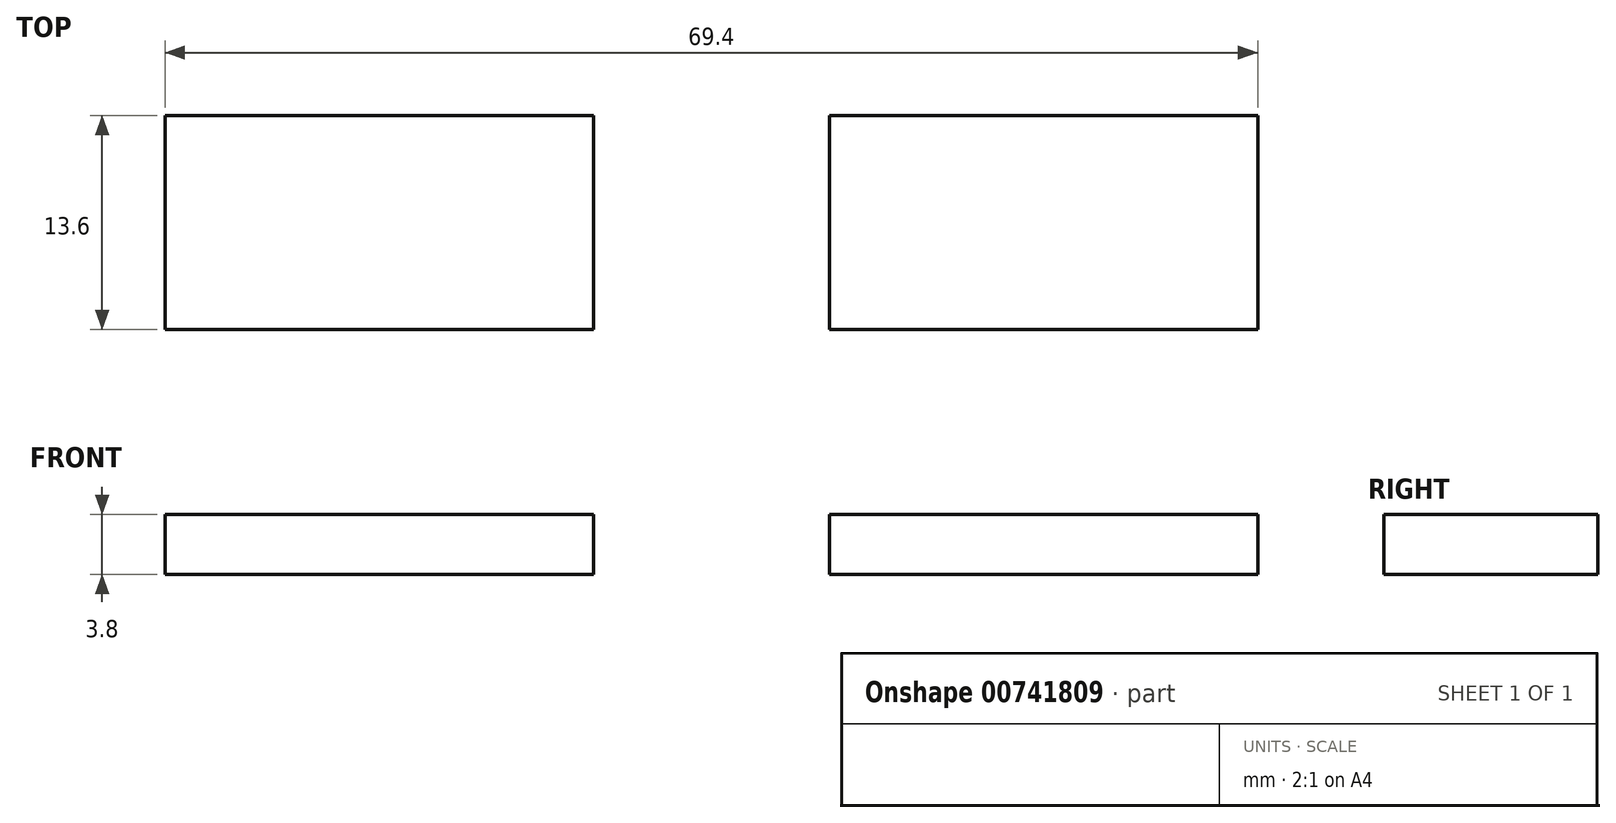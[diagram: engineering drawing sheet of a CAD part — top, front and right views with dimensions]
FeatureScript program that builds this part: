
annotation { "Feature Type Name" : "Feature", "Feature Type Description" : "" }
export const myFeature = defineFeature(function(context is Context, id is Id, definition is map)
    precondition{}
    {
        {
            var Q0;
            Q0=qCreatedBy(makeId("Top.planeOp"),FACE);
            var sketch = newSketch(context, id + "F0", { "sketchPlane" : qUnion([Q0])});
            skLineSegment(sketch, "E0.bottom", {"start": v(-220.8, 51.3) * mm, "end": v(229.2, 51.3) * mm});
            skLineSegment(sketch, "E0.top", {"start": v(-220.8, -98.7) * mm, "end": v(229.2, -98.7) * mm});
            skLineSegment(sketch, "E0.left", {"start": v(-220.8, 51.3) * mm, "end": v(-220.8, -98.7) * mm});
            skLineSegment(sketch, "E0.right", {"start": v(229.2, 51.3) * mm, "end": v(229.2, -98.7) * mm});
            skLineSegment(sketch, "E1", {"start": v(-152.8, -98.7) * mm, "end": v(-152.8, -85.1) * mm});
            skLineSegment(sketch, "E2", {"start": v(-152.8, -85.1) * mm, "end": v(-125.6, -85.1) * mm});
            skLineSegment(sketch, "E3", {"start": v(-125.6, -85.1) * mm, "end": v(-125.6, -98.7) * mm});
            skLineSegment(sketch, "E4", {"start": v(-125.6, -98.7) * mm, "end": v(-110.6, -98.7) * mm});
            skLineSegment(sketch, "E5", {"start": v(-110.6, -98.7) * mm, "end": v(-110.6, -85.1) * mm});
            skLineSegment(sketch, "E6", {"start": v(-110.6, -85.1) * mm, "end": v(-83.4, -85.1) * mm});
            skLineSegment(sketch, "E7", {"start": v(-83.4, -85.1) * mm, "end": v(-83.4, -98.7) * mm});
            skSolve(sketch);
        }
        {
            var Q0;
            {var subQ0=sQuery(id+"F0.wireOp",EDGE,"E1");Q0=makeQuery(id+"F0.imprint","IMPRINT",FACE,{"disambiguationData":[TD([[makeQuery(id+"F0.imprint","IMPRINT",EDGE,{"derivedFrom":subQ0}),-1.0]])]});}
            var Q1;
            {var subQ0=sQuery(id+"F0.wireOp",EDGE,"E5");Q1=makeQuery(id+"F0.imprint","IMPRINT",FACE,{"disambiguationData":[TD([[makeQuery(id+"F0.imprint","IMPRINT",EDGE,{"derivedFrom":subQ0}),-1.0]])]});}
            extrude(context, id + "F1", {"entities" : qUnion([Q0, Q1]), "depth" : 3.8 * mm, "offsetDistance" : 25 * mm});
        }
    });
